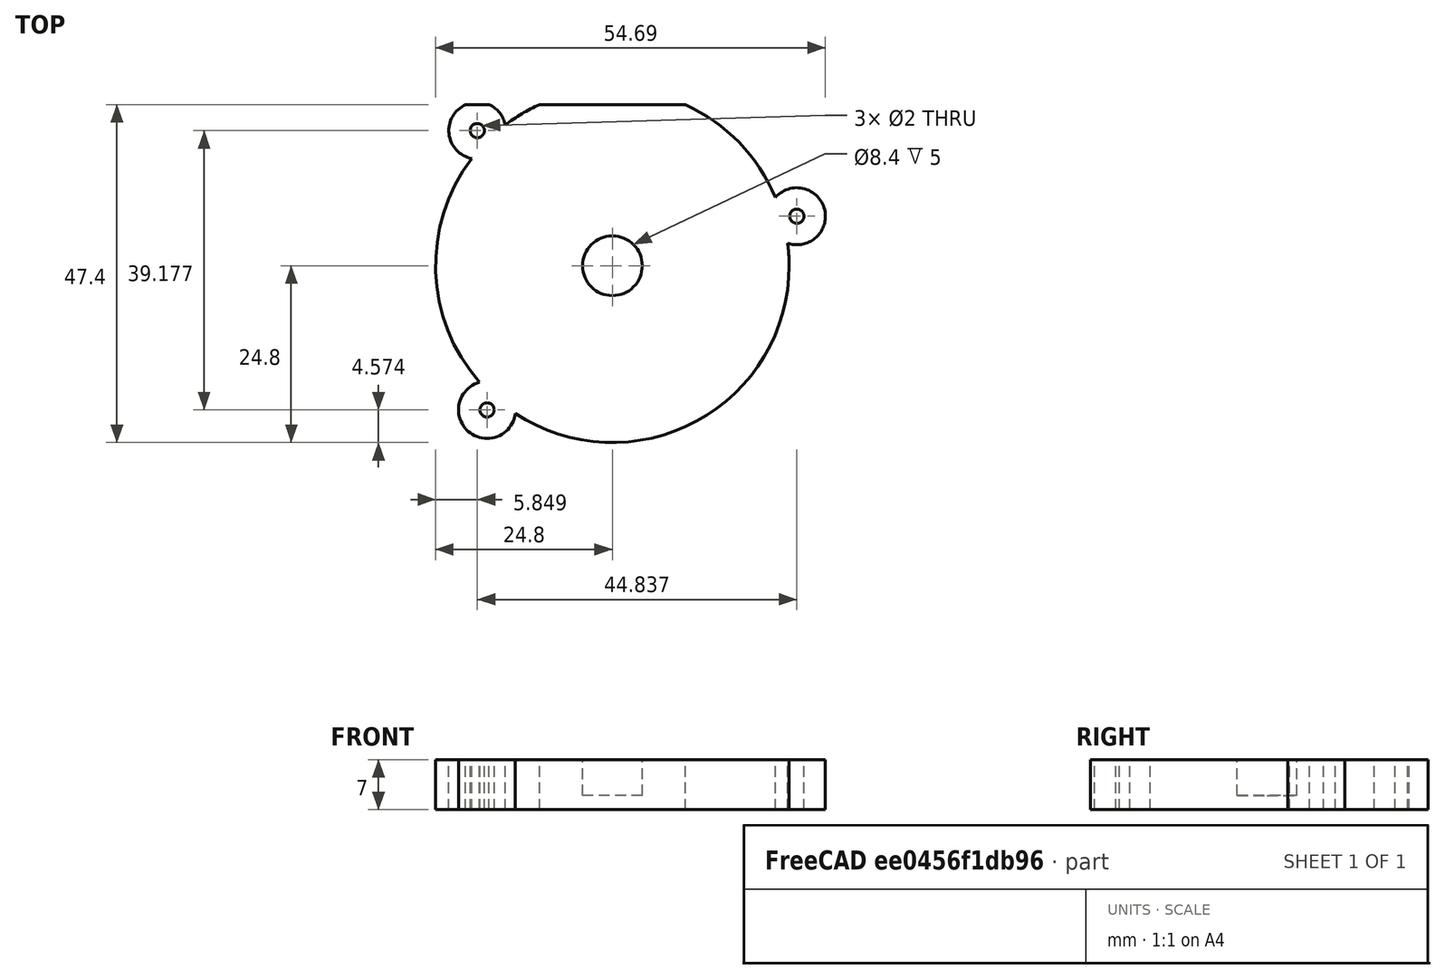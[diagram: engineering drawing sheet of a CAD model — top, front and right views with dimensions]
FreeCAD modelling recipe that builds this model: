
FCSTD DOCUMENT  (FreeCAD 0.18R16110 (Git))
Label: Gear_Cover
License: All rights reserved
LicenseURL: http://en.wikipedia.org/wiki/All_rights_reserved
objects: Part::Cut×6, Part::Cylinder×4, Part::MultiFuse×3, Part::Box×2, Spreadsheet::Sheet×1, Mesh::Feature×1
note: 15 computed .brp shape members not serialized (recipe doc carries the construction recipe); baked Part::Feature solids carry a one-line shape summary decoded from their .brp

FEATURE [Spreadsheet::Sheet] Spreadsheet
  cells = A1=Modul; B1(modul)=0.8; D1=tolerance; E1(tolerance)=0.2; G1=tolerance gear; H1(tolerance_gear)=0; A3=Zahnstange; D3=Zahnrad_1; G3=Zahnrad_2; J3=Ritzel; M3=Stepper; P3=Casing; A4=ra; B4(z_ra)=11; D4=#teeth; E4(z1_teeth)=16; G4=#teeth; H4(z2_teeth)=54; J4=#teeth; K4(ritzel_teeth)=16; M4=axis d; N4(stepper_daxis)=5; P4=gear casing sgear; Q4(casing_sgear)=2; A5=di; B5(z_ri)=8; D5=shift; E5(z1_shift)=0.2; G5=shift; H5(z2_shift)=0; J5=shift; K5(ritzel_shift)=0.3; M5=shaft l; N5(stepper_lshaft)=18; P5=rack casing srack; Q5(casing_srack)=2; A6=l; B6(z_l)==casing_ymax - casing_ymin + casing_scase; D6=pitch d; E6(z1_dpi)==modul * z1_teeth; G6=pitch d; H6(z2_dpi)==modul * z2_teeth; J6=pitch d; K6(ritzel_dpi)==modul * ritzel_teeth; M6=outside  sa; N6(stepper_sa)=28; P6=casing scase; Q6(casing_scase)=5; D7=outside d; E7(z1_da)==z1_dpi + 2 * (1 + z1_shift) * modul; G7=outside d; H7(z2_da)==z2_dpi + 2 * (1 + z2_shift) * modul; J7=outside d; K7(ritzel_da)==ritzel_dpi + 2 * (1 + ritzel_shift) * modul; M7=mount screw s; N7(stepper_sscrew)=23; P7=casing ssup; Q7(casing_ssup)=5; A8=rack height; B8(z_h)==z_th; D8=center distance; E8(z1_dc)==z1_dpi / 2 + z1_shift * modul + tolerance_gear; G8=center distance; H8(z2_dc)==z2_dpi / 2 + z2_shift * modul + tolerance_gear; J8=center distace; K8(ritzel_dc)==ritzel_dpi / 2 + ritzel_shift * modul + tolerance_gear; M8=mount d; N8(stepper_dmount)=22; P8=überlappung sjoin; Q8(casing_sjoin)=0.9; A9=rack thickness; B9(z_th)==2 * z_ra + 2; M9=mount heigth; N9(stepper_hmount)=2; A10=rack teeth width; B10(z_w)=8; D10=y Shift; E10(z1_yshift)=8; G10=height; H10(z2_h)=8; J10=angle z1; K10(ritzel_angle)=-65; M10=mount dscrew; N10(stepper_dscrew)=2.5; P10=casing y_min; Q10(casing_ymin)==-(Spreadsheet.z2_da / 2 + Spreadsheet.casing_scase + Spreadsheet.casing_sgear - Spreadsheet.z1_yshift - casing_sjoin + Spreadsheet.tolerance) * 0 + Spreadsheet.ritzel_ypos - stepper_sa / 2 - casing_scase; A11=#teeth; B11(z_teeth)=45; D11=height; E11(z1_height)==Spreadsheet.z_w * 3 / 4 + Spreadsheet.z2_dr + Spreadsheet.z2_h + Spreadsheet.z_ra; G11=distance rack; H11(z2_dr)=3; P11=casing x_min; Q11(casing_xmin)==-(Spreadsheet.z_ra * cos(asin(Spreadsheet.z_w / 2 / Spreadsheet.z_ra)) - Spreadsheet.modul + Spreadsheet.z_ra + Spreadsheet.casing_srack + Spreadsheet.casing_scase - Spreadsheet.casing_sjoin); D12=axis r; E12(z1_daxis)=2.5; G12=axis r; J12=x_pos; K12(ritzel_xpos)==Spreadsheet.z1_dc + cos(Spreadsheet.ritzel_angle) * (Spreadsheet.z2_dc + Spreadsheet.ritzel_dc); P12=casing z_min; Q12(casing_zmin)==-(Spreadsheet.z2_dr + Spreadsheet.z2_h - (Spreadsheet.z_h / 2 - Spreadsheet.z_ra) + Spreadsheet.tolerance) * 0 - 20.5; J13=y_pos; K13(ritzel_ypos)==Spreadsheet.z1_yshift + sin(Spreadsheet.ritzel_angle) * (Spreadsheet.z2_dc + Spreadsheet.ritzel_dc); G14=z_pos; H14(z2_zpos)==-(Spreadsheet.z2_dr + Spreadsheet.z2_h - (Spreadsheet.z_h / 2 - Spreadsheet.z_ra)); P14=casing z_max; Q14(casing_zmax)==(2 * Spreadsheet.casing_srack + Spreadsheet.z_th - Spreadsheet.casing_sjoin) * 0 + 44.5; G15=winkel 1; H15(z2_w1)==165°; P15=casing x_max; Q15(casing_xmax)==Spreadsheet.ritzel_xpos + stepper_sa / 2 + casing_scase + 2; A16=65; B16==-A16 / 2; C16==casing_xmax - casing_xmin - tolerance - casing_scase; G16=winkel 2; H16(z2_w2)==45°; P16=casing y_max; Q16(casing_ymax)==(Spreadsheet.ritzel_ypos + stepper_sa / 2 + 2) * 0 + 31; A17=8; B17==B16 + A18; C17==B17 ^ A20 * A19; G17=winkel 3; H17(z2_w3)==-49°; A18==A16 / A17; B18==B17 + A18; C18==B18 ^ A20 * A19; G18=winkel 4; H18(z2_w4)==-138°; A19==C16 / B16 ^ A20; B19==B18 + A18; C19==B19 ^ A20 * A19; A20=4; B20==B19 + A18; C20==B20 ^ A20 * A19; B21==B20 + A18; C21==B21 ^ A20 * A19; B22==B21 + A18; C22==B22 ^ A20 * A19; B23==B22 + A18; C23==B23 ^ A20 * A19; B24==B23 + A18; C24==B24 ^ A20 * A19
FEATURE [Part::Cylinder] Cylinder127  label="Zylinder127"
  Angle = 360
  AttacherType = Attacher::AttachEngine3D
  Height = 7
  Radius = 4
FEATURE [Part::Cylinder] Cylinder118  label="Zylinder118"
  Angle = 360
  AttacherType = Attacher::AttachEngine3D
  Height = 7
  Radius = 24.8
  expr: Radius = Spreadsheet.z2_da / 2 + Spreadsheet.tolerance * 2 + Spreadsheet.casing_sgear
FEATURE [Part::Cylinder] Cylinder126  label="Zylinder126"
  Angle = 360
  AttacherType = Attacher::AttachEngine3D
  Height = 5.2
  Placement = pos=(0,0,2) rot=(0,0,1;0rad)
  Radius = 4.2
  expr: Placement.Base.z = Spreadsheet.casing_sgear
  expr: Height = 5 + Spreadsheet.tolerance
  expr: Radius = 4 + Spreadsheet.tolerance
FEATURE [Part::Cut] Cut093
  Base = -> Cylinder118
  Tool = -> Cylinder126
FEATURE [Part::Box] Box017  label="Quader012"
  AttacherType = Attacher::AttachEngine3D
  Height = 7
  Length = 50
  Placement = pos=(-26.547,30.6,-30) rot=(0,0,1;0rad)
  Width = 5
  expr: Placement.Base.y = Spreadsheet.casing_ymax - Spreadsheet.tolerance * 2
  expr: Placement.Base.x = Spreadsheet.casing_xmin
  expr: Width = Spreadsheet.casing_scase
FEATURE [Part::Box] Box018  label="Boden002"
  AttacherType = Attacher::AttachEngine3D
  Height = 7
  Length = 50
  Placement = pos=(-26.547,-36.1941,-30) rot=(0,0,1;0rad)
  Width = 5
  expr: Placement.Base.y = Spreadsheet.casing_ymin + Spreadsheet.tolerance * 2
  expr: Placement.Base.x = Spreadsheet.casing_xmin
  expr: Width = Spreadsheet.casing_scase
FEATURE [Part::Cylinder] Cylinder128  label="Zylinder128"
  Angle = 360
  AttacherType = Attacher::AttachEngine3D
  Height = 7
  Radius = 1
FEATURE [Part::Cut] Cut094
  Base = -> Cylinder127
  Placement = pos=(25.8868,6.93635,0) rot=(0,0,1;0rad)
  Tool = -> Cylinder128
  expr: Placement.Base.y = (Spreadsheet.z2_da / 2 + Spreadsheet.tolerance * 2 + Spreadsheet.casing_sgear + 2) * sin(Spreadsheet.z2_w1)
  expr: Placement.Base.x = -(Spreadsheet.z2_da / 2 + Spreadsheet.tolerance * 2 + Spreadsheet.casing_sgear + 2) * cos(Spreadsheet.z2_w1)
FEATURE [Part::Cut] Cut096
  Base = -> Cylinder127
  Placement = pos=(-17.5824,-20.2262,0) rot=(0,0,1;0rad)
  Tool = -> Cylinder128
  expr: Placement.Base.y = (Spreadsheet.z2_da / 2 + Spreadsheet.tolerance * 2 + Spreadsheet.casing_sgear + 2) * sin(Spreadsheet.z2_w3)
  expr: Placement.Base.x = -(Spreadsheet.z2_da / 2 + Spreadsheet.tolerance * 2 + Spreadsheet.casing_sgear + 2) * cos(Spreadsheet.z2_w3)
FEATURE [Part::Cut] Cut095
  Base = -> Cylinder127
  Placement = pos=(-18.9505,18.9505,0) rot=(0,0,1;0rad)
  Tool = -> Cylinder128
  expr: Placement.Base.y = (Spreadsheet.z2_da / 2 + Spreadsheet.tolerance * 2 + Spreadsheet.casing_sgear + 2) * sin(Spreadsheet.z2_w2)
  expr: Placement.Base.x = -(Spreadsheet.z2_da / 2 + Spreadsheet.tolerance * 2 + Spreadsheet.casing_sgear + 2) * cos(Spreadsheet.z2_w2)
FEATURE [Part::MultiFuse] Fusion044
  Shapes = -> [Cut093,Cut094]
FEATURE [Part::MultiFuse] Fusion045
  Shapes = -> [Fusion044,Cut095]
FEATURE [Part::MultiFuse] Fusion046  label="Deckel"
  Placement = pos=(6.56,8,-30) rot=(0,0,1;0rad)
  Shapes = -> [Fusion045,Cut096]
  expr: Placement.Base.z = Spreadsheet.z2_zpos - 20
  expr: Placement.Base.y = Spreadsheet.z1_yshift
  expr: Placement.Base.x = Spreadsheet.z1_dc + Spreadsheet.tolerance_gear
FEATURE [Part::Cut] Cut097
  Base = -> Fusion046
  Tool = -> Box017
FEATURE [Part::Cut] Cut098  label="Gear_Cover"
  Base = -> Cut097
  Placement = pos=(0,0,13) rot=(0,0,1;0rad)
  Tool = -> Box018
FEATURE [Mesh::Feature] Mesh  label="Gear_Cover (Meshed)"
